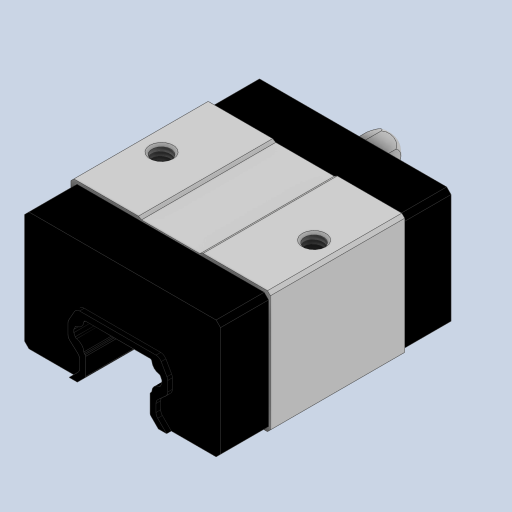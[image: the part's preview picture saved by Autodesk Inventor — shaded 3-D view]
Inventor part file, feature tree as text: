
AUTODESK INVENTOR PART (.ipt)
format: ipt  version: 2023 (Build 270158000, 158)  size: 606,720 bytes
history: native  units: mm
features: sketch x13, extrude x10, other x7, hole x2, revolve x1
ambient origin geometry x8: Origin, YZ Plane, XZ Plane, XY Plane, X Axis, Y Axis, Z Axis, Center Point
bodies: Solid1 (feature_tree)
feature tree (33):
  extrude  "Extrusion1"  Depth=39.3mm TaperAngle=0.0deg
  extrude  "Extrusion2"  Depth=7.0mm TaperAngle=0.0deg
  revolve  "Revolution1"  [1 undecoded]
  extrude  "Extrusion3"  Depth=11.45mm TaperAngle=0.0deg
  extrude  "Extrusion4"  Depth=0.05mm TaperAngle=0.0deg
  extrude  "Extrusion5"  [1 undecoded]
  extrude  "Extrusion6"  [1 undecoded]
  extrude  "Extrusion7"  [1 undecoded]
  extrude  "Extrusion8"  [1 undecoded]
  hole  "Hole1"  [1 undecoded]
  hole  "Hole2"  [1 undecoded]
  extrude  "Extrusion9"  [1 undecoded]
  extrude  "Extrusion10"  [1 undecoded]
  other  "to_rail_XY"
  other  "to_rail_YZ"
  other  "to_rail_ZX"
  other  "to_rail_X"
  other  "to_rail_Y"
  other  "to_rail_Z"
  other  "to_rail_Center"
  sketch  "Sketch_1"  dims[d0=22.9mm d1=0.0mm d2=39.3mm d3=0.0mm]
  sketch  "Sketch_2"  dims[d4=360.0deg d5=7.0mm d6=0.0mm]
  sketch  "Sketch_32"
  sketch  "Sketch_33"
  sketch  "Sketch_7"  dims[d11=22.9mm d12=0.0mm d13=11.45mm d14=0.0mm]
  sketch  "Sketch_10"  dims[d15=11.45mm d16=0.0mm]
  sketch  "Sketch_3"  dims[d7=0.8mm d8=0.0mm d9=0.8mm d10=0.0mm]
  sketch  "Sketch_11"  dims[d24=3.242mm d25=5.0mm d26=4.0mm d27=2.0mm d28=90.0deg d29=7.1mm d30=120.0deg d31=0.05mm d32=0.0mm]
  sketch  "Sketch_12"
  sketch  "Sketch10"  dims[d17=3.242mm d18=5.0mm d19=4.0mm d20=2.0mm d21=90.0deg d22=7.1mm d23=120.0deg]
  sketch  "Sketch11"  dims[d33=0.05mm d34=0.0mm]
  sketch  "Sketch_29"
  sketch  "Sketch_30"
note: 9 required parameter values undecoded (feature->parameter linkage not recoverable at this tier; creation-order binding heuristic only, values carry confidence <= 0.55)